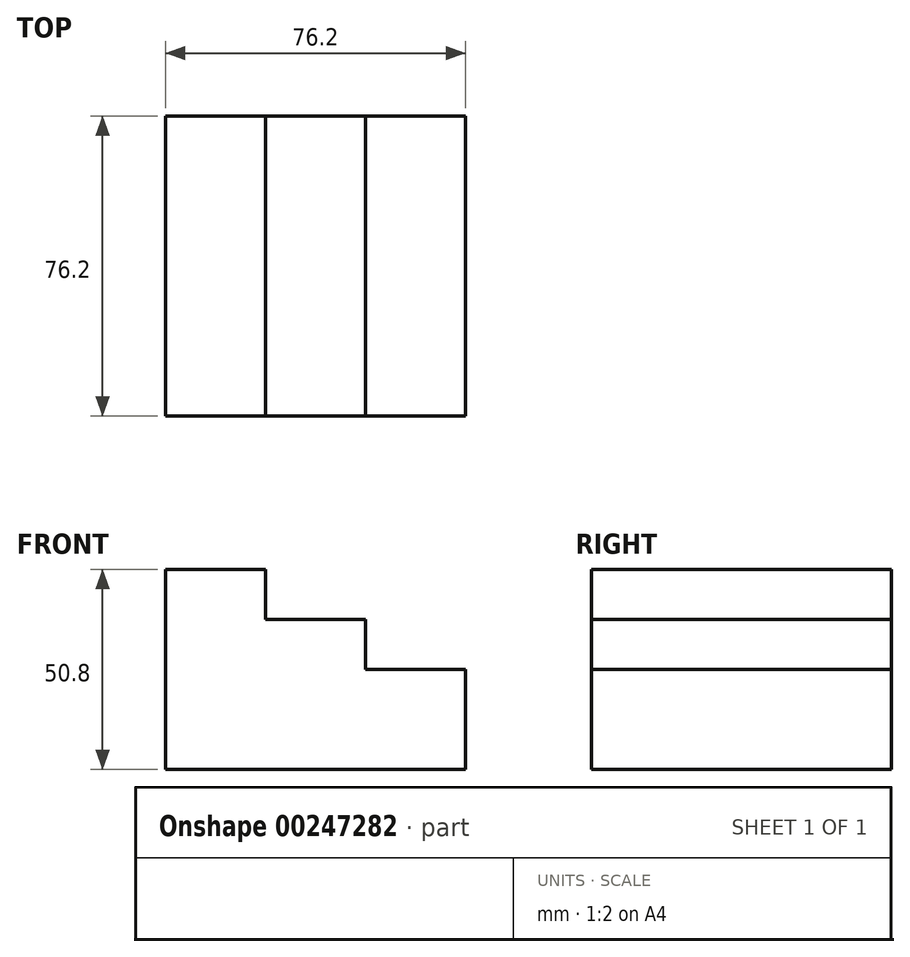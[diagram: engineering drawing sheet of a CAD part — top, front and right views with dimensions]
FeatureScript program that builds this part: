
annotation { "Feature Type Name" : "Feature", "Feature Type Description" : "" }
export const myFeature = defineFeature(function(context is Context, id is Id, definition is map)
    precondition{}
    {
        {
            var Q0;
            Q0=qCreatedBy(makeId("Front.planeOp"),FACE);
            var sketch = newSketch(context, id + "F0", { "sketchPlane" : qUnion([Q0])});
            skLineSegment(sketch, "E0", {"start": v(0, 0) * mm, "end": v(0, 50.8) * mm});
            skLineSegment(sketch, "E1", {"start": v(0, 50.8) * mm, "end": v(25.4, 50.8) * mm});
            skLineSegment(sketch, "E2", {"start": v(25.4, 50.8) * mm, "end": v(25.4, 38.1) * mm});
            skLineSegment(sketch, "E3", {"start": v(25.4, 38.1) * mm, "end": v(50.8, 38.1) * mm});
            skLineSegment(sketch, "E4", {"start": v(50.8, 38.1) * mm, "end": v(50.8, 25.4) * mm});
            skLineSegment(sketch, "E5", {"start": v(50.8, 25.4) * mm, "end": v(76.2, 25.4) * mm});
            skLineSegment(sketch, "E6", {"start": v(76.2, 25.4) * mm, "end": v(76.2, 0) * mm});
            skLineSegment(sketch, "E7", {"start": v(0, 0) * mm, "end": v(76.2, 0) * mm});
            skSolve(sketch);
        }
        {
            var Q0;
            Q0=makeQuery(id+"F0.imprint","IMPRINT",FACE,{"disambiguationData":[TD([[makeQuery(id+"F0.imprint","IMPRINT",EDGE,{"derivedFrom":sQuery(id+"F0.wireOp",EDGE,"E0")}),-1.0]])]});
            extrude(context, id + "F1", {"entities" : qUnion([Q0]), "oppositeDirection" : true, "depth" : 76.2 * mm});
        }
    });
